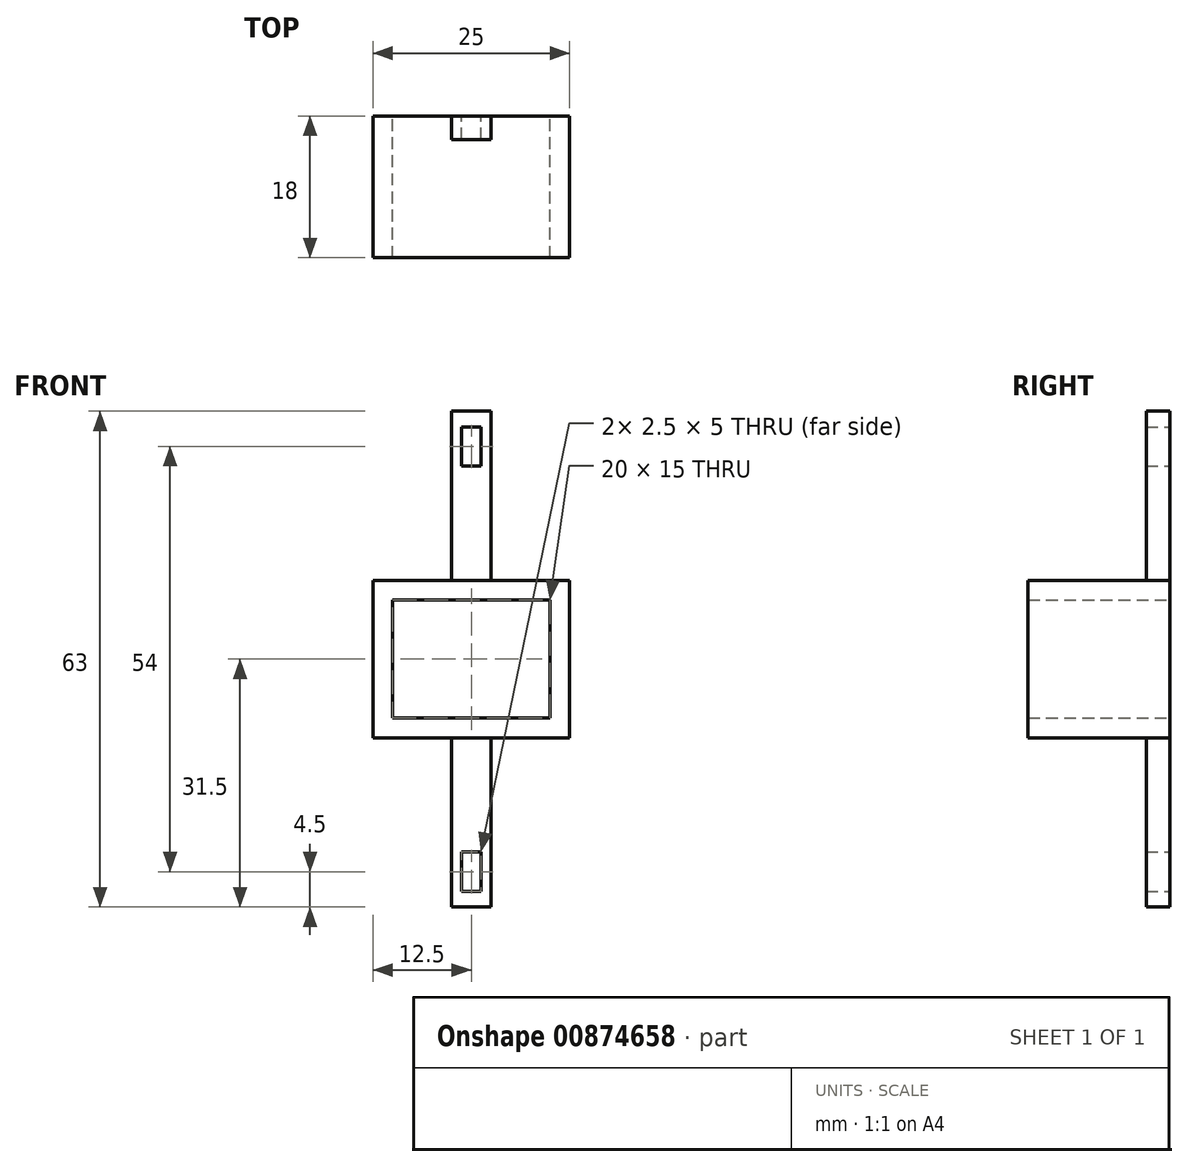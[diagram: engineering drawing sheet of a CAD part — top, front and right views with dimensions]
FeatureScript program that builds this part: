
annotation { "Feature Type Name" : "Feature", "Feature Type Description" : "" }
export const myFeature = defineFeature(function(context is Context, id is Id, definition is map)
    precondition{}
    {
        {
            var Q0;
            Q0=qCreatedBy(makeId("Front.planeOp"),FACE);
            var sketch = newSketch(context, id + "F0", { "sketchPlane" : qUnion([Q0])});
            skLineSegment(sketch, "E0.bottom", {"start": v(10, -7.5) * mm, "end": v(-10, -7.5) * mm});
            skLineSegment(sketch, "E0.top", {"start": v(10, 7.5) * mm, "end": v(-10, 7.5) * mm});
            skLineSegment(sketch, "E0.left", {"start": v(10, -7.5) * mm, "end": v(10, 7.5) * mm});
            skLineSegment(sketch, "E0.right", {"start": v(-10, -7.5) * mm, "end": v(-10, 7.5) * mm});
            skPoint(sketch, "E0.middle", {"position": v(0, 0) * mm});
            skLineSegment(sketch, "E1.bottom", {"start": v(12.5, -10) * mm, "end": v(-12.5, -10) * mm});
            skLineSegment(sketch, "E1.top", {"start": v(12.5, 10) * mm, "end": v(-12.5, 10) * mm});
            skLineSegment(sketch, "E1.left", {"start": v(12.5, -10) * mm, "end": v(12.5, 10) * mm});
            skLineSegment(sketch, "E1.right", {"start": v(-12.5, -10) * mm, "end": v(-12.5, 10) * mm});
            skLineSegment(sketch, "E2.bottom", {"start": v(2.5, -31.5) * mm, "end": v(-2.5, -31.5) * mm});
            skLineSegment(sketch, "E2.top", {"start": v(2.5, 31.5) * mm, "end": v(-2.5, 31.5) * mm});
            skLineSegment(sketch, "E2.left", {"start": v(2.5, -31.5) * mm, "end": v(2.5, 31.5) * mm});
            skLineSegment(sketch, "E2.right", {"start": v(-2.5, -31.5) * mm, "end": v(-2.5, 31.5) * mm});
            skLineSegment(sketch, "E3.bottom", {"start": v(1.25, -24.5) * mm, "end": v(-1.25, -24.5) * mm});
            skLineSegment(sketch, "E3.top", {"start": v(1.25, -29.5) * mm, "end": v(-1.25, -29.5) * mm});
            skLineSegment(sketch, "E3.left", {"start": v(1.25, -24.5) * mm, "end": v(1.25, -29.5) * mm});
            skLineSegment(sketch, "E3.right", {"start": v(-1.25, -24.5) * mm, "end": v(-1.25, -29.5) * mm});
            skPoint(sketch, "E3.middle", {"position": v(0, -27) * mm});
            skLineSegment(sketch, "E4.bottom", {"start": v(1.25, 24.5) * mm, "end": v(-1.25, 24.5) * mm});
            skLineSegment(sketch, "E4.top", {"start": v(1.25, 29.5) * mm, "end": v(-1.25, 29.5) * mm});
            skLineSegment(sketch, "E4.left", {"start": v(1.25, 24.5) * mm, "end": v(1.25, 29.5) * mm});
            skLineSegment(sketch, "E4.right", {"start": v(-1.25, 24.5) * mm, "end": v(-1.25, 29.5) * mm});
            skPoint(sketch, "E4.middle", {"position": v(0, 27) * mm});
            skSolve(sketch);
        }
        {
            var Q0;
            {var subQ1=sQuery(id+"F0.wireOp",EDGE,"E2.top");Q0=makeQuery(id+"F0.imprint","IMPRINT",FACE,{"disambiguationData":[TD([[makeQuery(id+"F0.imprint","IMPRINT",EDGE,{"derivedFrom":subQ1}),1.0]])]});}
            var Q1;
            {var subQ1=sQuery(id+"F0.wireOp",EDGE,"E2.bottom");Q1=makeQuery(id+"F0.imprint","IMPRINT",FACE,{"disambiguationData":[TD([[makeQuery(id+"F0.imprint","IMPRINT",EDGE,{"derivedFrom":subQ1}),-1.0]])]});}
            extrude(context, id + "F1", {"entities" : qUnion([Q0, Q1]), "depth" : 3 * mm, "offsetDistance" : 25 * mm});
        }
        {
            var Q0;
            {var subQ0=sQuery(id+"F0.wireOp",EDGE,"E2.left");var subQ1=sQuery(id+"F0.wireOp",EDGE,"E0.top");var subQ2=makeQuery(id+"F0.imprint","INTERSECT",VERTEX,{"derivedFrom":[subQ1,subQ0]});Q0=makeQuery(id+"F0.imprint","IMPRINT",FACE,{"disambiguationData":[TD([[makeQuery(id+"F0.imprint","IMPRINT",EDGE,{"disambiguationData":[TD([[subQ2,-1.0]])],"derivedFrom":subQ1}),-1.0]])]});}
            var Q1;
            {var subQ0=sQuery(id+"F0.wireOp",EDGE,"E0.left");Q1=makeQuery(id+"F0.imprint","IMPRINT",FACE,{"disambiguationData":[TD([[makeQuery(id+"F0.imprint","IMPRINT",EDGE,{"derivedFrom":subQ0}),-1.0]])]});}
            var Q2;
            {var subQ0=sQuery(id+"F0.wireOp",EDGE,"E2.left");var subQ1=sQuery(id+"F0.wireOp",EDGE,"E0.bottom");var subQ2=makeQuery(id+"F0.imprint","INTERSECT",VERTEX,{"derivedFrom":[subQ1,subQ0]});Q2=makeQuery(id+"F0.imprint","IMPRINT",FACE,{"disambiguationData":[TD([[makeQuery(id+"F0.imprint","IMPRINT",EDGE,{"disambiguationData":[TD([[subQ2,-1.0]])],"derivedFrom":subQ1}),1.0]])]});}
            var Q3;
            {var subQ4=sQuery(id+"F0.wireOp",EDGE,"E0.right");Q3=makeQuery(id+"F0.imprint","IMPRINT",FACE,{"disambiguationData":[TD([[makeQuery(id+"F0.imprint","IMPRINT",EDGE,{"derivedFrom":subQ4}),1.0]])]});}
            extrude(context, id + "F2", {"entities" : qUnion([Q0, Q1, Q2, Q3]), "depth" : 18 * mm, "offsetDistance" : 25 * mm});
        }
    });
